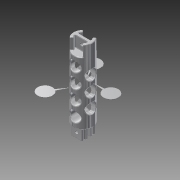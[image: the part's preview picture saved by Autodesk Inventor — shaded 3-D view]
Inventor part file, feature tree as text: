
AUTODESK INVENTOR PART (.ipt)
format: ipt  version: 2014 (Build 180170000, 170)  size: 1,066,496 bytes
history: native  units: mm
features: extrude x8, sketch x5, plane x3, other x2, fillet x2, folder x1, mirror x1
ambient origin geometry x8: Origin, YZ Plane, XZ Plane, XY Plane, X Axis, Y Axis, Z Axis, Center Point
bodies: Solid1 (feature_tree)
feature tree (22):
  folder  "Master Lengths"
  other  "Profile"
  extrude  "Plug Side"  Depth=2.0mm
  extrude  "Fuse Section"  TaperAngle=45.0deg  [1 undecoded]
  plane  "Work Plane2"
  extrude  "Clamp Side Extrude"  Depth=15.0mm TaperAngle=0.0deg
  fillet  "Fillet1"  Radius=85.0mm
  extrude  "Extrusion4"  Depth=12.0mm
  extrude  "Extrusion5"  Depth=0.6mm
  fillet  "Fillet4"  Radius=15.0mm
  extrude  "Extrusion6"  Depth=0.6mm
  plane  "Work Plane3"
  plane  "Work Plane4"
  sketch  "Sketch7"  dims[d11=0.0mm d12=12.0mm]
  sketch  "Sketch8"  dims[d13=12.0mm d14=15.0mm d16=15.0mm d18=100.0mm d19=25.0mm d21=85.0mm d23=-85.0mm d24=15.0mm d25=0.0mm d26=1.0mm d27=1.0mm d28=6.0mm d29=0.0mm d32=40.0mm d33=0.0mm d37=0.0mm d41=14.0mm d42=14.0mm d43=12.8mm d44=85.0mm d45=12.8mm d47=14.0mm d49=22.7mm d50=22.7mm d51=40.0mm d52=0.0mm d54=4.0mm d56=4.0mm d57=7.5mm d58=7.5mm d59=7.5mm d60=7.5mm d61=0.0mm d62=0.0mm d63=20.0mm d64=0.0mm d65=14.0mm d66=14.0mm d67=19.8mm d68=19.8mm d69=14.0mm d70=14.0mm d71=2.9mm d72=2.9mm d73=2.9mm d74=2.9mm d75=1.0mm d76=26.0mm d77=-32.75mm d78=-42.5mm d79=26.0mm d80=1.570796mm d81=0.785398mm d82=15.0mm d83=15.0mm d84=10.0mm d85=26.0mm d86=120.0deg d87=120.0deg d88=1.570796mm d89=0.785398mm d90=15.0mm d91=10.0mm d92=0.6mm d93=0.0mm d94=0.6mm d95=0.0mm]
  extrude  "Extrusion7"  Depth=0.6mm
  extrude  "Extrusion8"  Depth=0.6mm
  mirror  "Mirror1"
  other  "Clamp Side"
  sketch  "Sketch4"  dims[d0=4.0mm d2=2.0mm]
  sketch  "Sketch5"  dims[d4=4.0mm d5=45.0deg]
  sketch  "Sketch6"  dims[d6=45.0deg d7=15.0mm d8=0.0mm d9=85.0mm d10=0.0mm]
note: 1 required parameter value undecoded (feature->parameter linkage not recoverable at this tier; creation-order binding heuristic only, values carry confidence <= 0.55)
